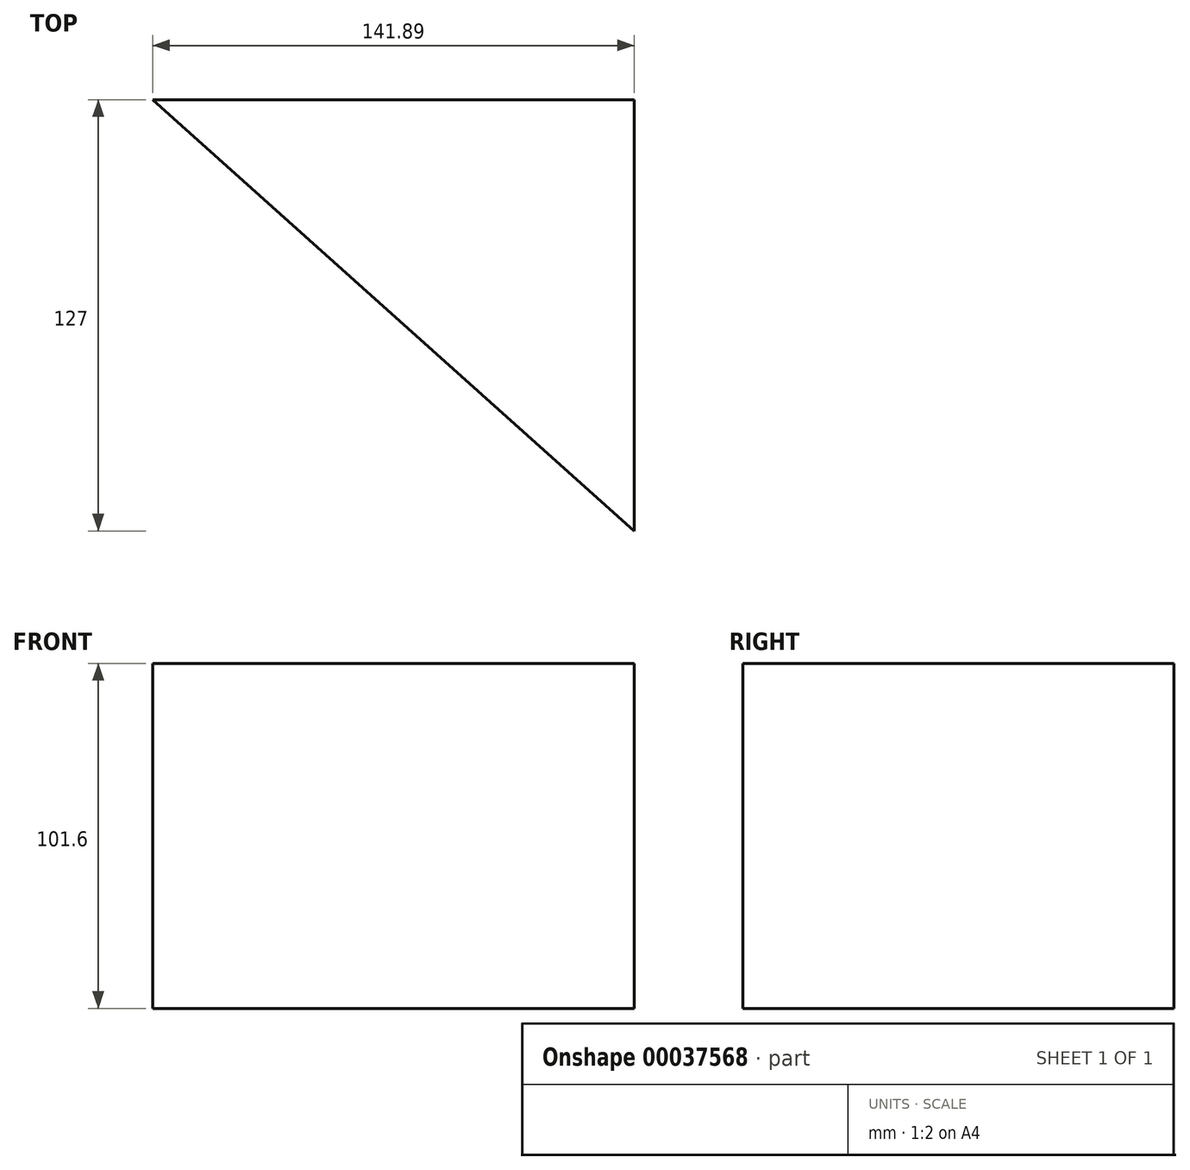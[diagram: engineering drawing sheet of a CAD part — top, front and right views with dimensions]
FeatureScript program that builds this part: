
annotation { "Feature Type Name" : "Feature", "Feature Type Description" : "" }
export const myFeature = defineFeature(function(context is Context, id is Id, definition is map)
    precondition{}
    {
        {
            var Q0;
            Q0=qCreatedBy(makeId("Top.planeOp"),FACE);
            var sketch = newSketch(context, id + "F0", { "sketchPlane" : qUnion([Q0])});
            skLineSegment(sketch, "E0.bottom", {"start": v(0, 0) * mm, "end": v(141.89, 0) * mm});
            skLineSegment(sketch, "E0.top", {"start": v(0, 127) * mm, "end": v(141.89, 127) * mm});
            skLineSegment(sketch, "E0.left", {"start": v(0, 0) * mm, "end": v(0, 127) * mm});
            skLineSegment(sketch, "E0.right", {"start": v(141.89, 0) * mm, "end": v(141.89, 127) * mm});
            skLineSegment(sketch, "E1", {"start": v(0, 127) * mm, "end": v(141.89, 0) * mm});
            skSolve(sketch);
        }
        {
            var Q0;
            Q0=makeQuery(id+"F0.imprint","IMPRINT",FACE,{"disambiguationData":[TD([[makeQuery(id+"F0.imprint","IMPRINT",EDGE,{"derivedFrom":sQuery(id+"F0.wireOp",EDGE,"E0.top")}),-1.0]])]});
            extrude(context, id + "F1", {"entities" : qUnion([Q0]), "depth" : 101.6 * mm});
        }
    });
